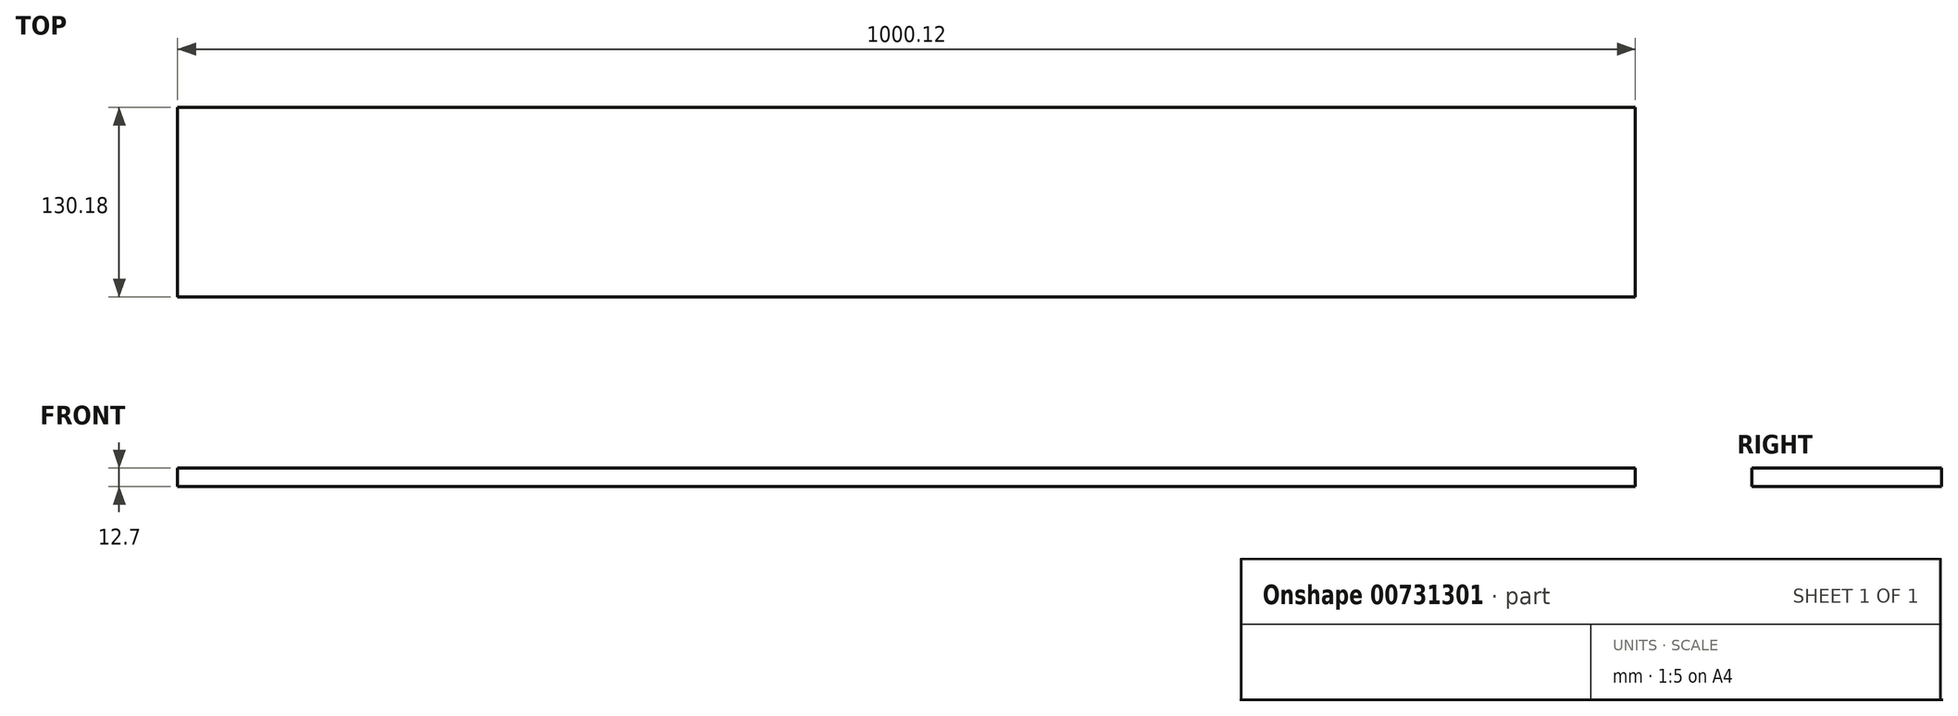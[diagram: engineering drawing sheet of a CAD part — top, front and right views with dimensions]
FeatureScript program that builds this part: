
annotation { "Feature Type Name" : "Feature", "Feature Type Description" : "" }
export const myFeature = defineFeature(function(context is Context, id is Id, definition is map)
    precondition{}
    {
        {
            var Q0;
            Q0=qCreatedBy(makeId("Top.planeOp"),FACE);
            var sketch = newSketch(context, id + "F0", { "sketchPlane" : qUnion([Q0])});
            skLineSegment(sketch, "E0.bottom", {"start": v(0, 0) * mm, "end": v(1000.13, 0) * mm});
            skLineSegment(sketch, "E0.top", {"start": v(0, 130.18) * mm, "end": v(1000.13, 130.18) * mm});
            skLineSegment(sketch, "E0.left", {"start": v(0, 0) * mm, "end": v(0, 130.18) * mm});
            skLineSegment(sketch, "E0.right", {"start": v(1000.13, 0) * mm, "end": v(1000.13, 130.18) * mm});
            skSolve(sketch);
        }
        {
            var Q0;
            Q0=makeQuery(id+"F0.imprint","IMPRINT",FACE,{"disambiguationData":[TD([[makeQuery(id+"F0.imprint","IMPRINT",EDGE,{"derivedFrom":sQuery(id+"F0.wireOp",EDGE,"E0.bottom")}),1.0]])]});
            extrude(context, id + "F1", {"entities" : qUnion([Q0]), "depth" : 12.7 * mm, "offsetDistance" : 25.4 * mm});
        }
    });
